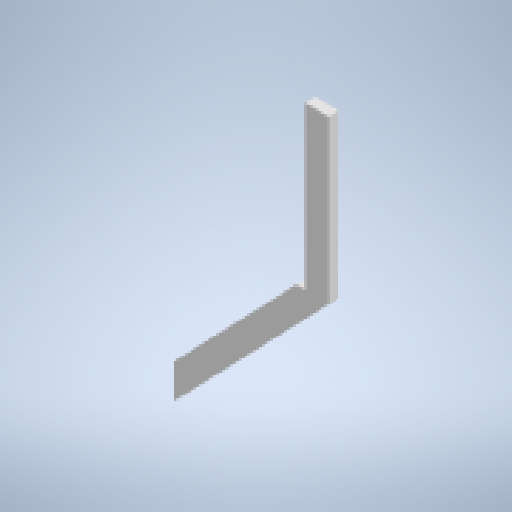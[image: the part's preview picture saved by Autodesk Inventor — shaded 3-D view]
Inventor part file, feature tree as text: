
AUTODESK INVENTOR PART (.ipt)
format: ipt  version: 2025.1 (Build 291241020, 241B)  size: 136,704 bytes
history: native  units: in
note: dims shown in document units (in); Inventor stores cm internally (conversion verified against a paired STEP export)
features: other x5, reference x3, extrude x1, sketch x1
ambient origin geometry x8: Origin, YZ Plane, XZ Plane, XY Plane, X Axis, Y Axis, Z Axis, Center Point
bodies: Solid1 (feature_tree)
feature tree (10):
  extrude  "Extrusion1"  [1 undecoded]
  sketch  "Sketch1"  dims[d2=1.5in d3=0.0in]
  reference  "Reference1"
  reference  "Reference2"
  reference  "Reference3"
  other  "<userpath>\Documents\Tburn24\F_Legs2\F_Legs2.iam"
  other  "F_Legs2.iam"
  other  "8'x2x4:4"
  other  "4x2x4:6"
  other  "3'5x2x4:4"
note: 1 required parameter value undecoded (feature->parameter linkage not recoverable at this tier; creation-order binding heuristic only, values carry confidence <= 0.55)
